# Revit family: 277V DOBLE 5050 IP65_L14277UWW
name_source: partatom
category: Luminarias
units: mm (PartAtom-declared; Revit-internal decimal feet)

## family parameters
Compartido = No
Corte con vacíos al cargar = No
Cota de conector redondo = Diámetro de uso
Origen de luz = Sí
Punto de cálculo de habitación = No
Se basa en plano de trabajo = Sí
Siempre vertical = No
Tipo de pieza = Normal

## types (1)
- 277V DOBLE 5050 IP65_L14277UWW
    Archivo de red fotométrica = L14277UWW_277V DOBLE 5050 IP65.IES
    Cambio de temperatura de color de luz atenuada = <Ninguno>
    Comentarios de vataje = 277V
    Costo = 0 $
    Descripción = TIRA LED DOBLE DE PCB CON RECUBRIMIENTO DE PLASTICO 21MM MONOCROMATICA , CON UNA POTENCIA DE 20W/M DE UN TIPO DE LED 5050 SMD, USO PARA INTERIORES COMO EXTERIORES IP65, IRC80, 120 LEDS POR METRO, PRESENTACION DE 50M, TEMPERATURA EN BLANCO ULTRA CALIDO 2400K, 1019 LUMENES POR METRO, EFICIENCIA DE 50.95 LM/W, CORTE A 50CM, ALIMENTADA A 277V, REQUIERE ACCESORIOS COMO CONVERTIDOR DE CORRIENTE (1 POR SEGMENTO DE TIRA), CONECTOR INTERMEDIO (CONSIDERAR EN CORTES DE TIRA O ANGULOS CERRADOS), CONECTOR AGUJA (CONSIDERAR 1PZA PRO CADA CONVERTIDOR), FUNDA TERMOCONTRACTIL (CONSIDERAR 2PZAS POR SEGMENTO DE TIRA), TAPA FINAL (CONSIDERAR 1PZA POR SEGMENTO DE TIRA) Y CLIPS DE SUJECION (CONSIDERAR 4 PZAS POR 1M)
    Elevación por defecto = 0 mm  [stored 0 ft]
    Fabricante = BRILLANT
    Filtro de color = 16777215
    Longitud de línea de emisión = 600 mm
    Lámpara = 5050 SMD
    Modelo = L14277UWW
    Ángulo de inclinación = 60.00°

note: [stored X ft] marks values corroborated as IEEE doubles in the binary element streams (Revit-internal decimal feet)

## geometry (parser evidence)
native form markers: Blend x2
no freeform markers — native parametric forms only
